# Revit family: Faucet-Lavatory-KOHLER-COMPOSED-K-73067T_1
name_source: partatom
category: Plumbing Fixtures
revit_build: Autodesk Revit 2017 (Build: 20160225_1515(x64)
units: mm (PartAtom-declared; Revit-internal decimal feet)

## family parameters
Cut with Voids When Loaded = No
Host = Face
OmniClass Number = 23.31.11.00
OmniClass Title = Faucets
Part Type = Normal
Room Calculation Point = No
Round Connector Dimension = Use Diameter
Shared = No

## types (1)
- Not a Type-See Type Catalog
    1 = 1"
    ADA Compliant = No
    Assembly Code = D2010
    CW Connection = Yes
    Cold Water Inlet = Cold Water Inlet
    Cross Handle = Yes
    Date Modified = 05/27/2020
    Default Elevation = 36"
    Description = Bai Shi double wall water washbasin faucet cross handle
    Dist_1 = 1 1/2"
    Drain Included = Yes
    Finish = Default
    Flow Rate = 0 GPM
    Glass Handle = No
    HW Connection = Yes
    Handle Clearance = 1 1/2"
    Handle Material = Default
    Height = 2"
    Hot Water Inlet = Hot Water Inlet
    Length = 8 1/2"
    Lever Handle = No
    Manufacturer = KOHLER Co
    MasterFormat 1995 = 15410
    MasterFormat 2004 = 22.41.39
    Material = Premium Material Construction
    Model = K-73067T-3-RGD
    Pressure = 116.00 psi
    Product Documentation Link = http://files.kohler.com.cn
    Product Name = Composed
    Product Page URL = http://www.kohler.com.cn
    Spout Reach = 8 1/2"
    Type = 1
    URL = http://www.kohler.com.cn
    Vent Connection = No
    Waste Connection = No
    Waste Water Outlet = Waste Water Outlet
    WaterSense Certified = No

## geometry (parser evidence)
native form markers: Sweep x4
no freeform markers — native parametric forms only
